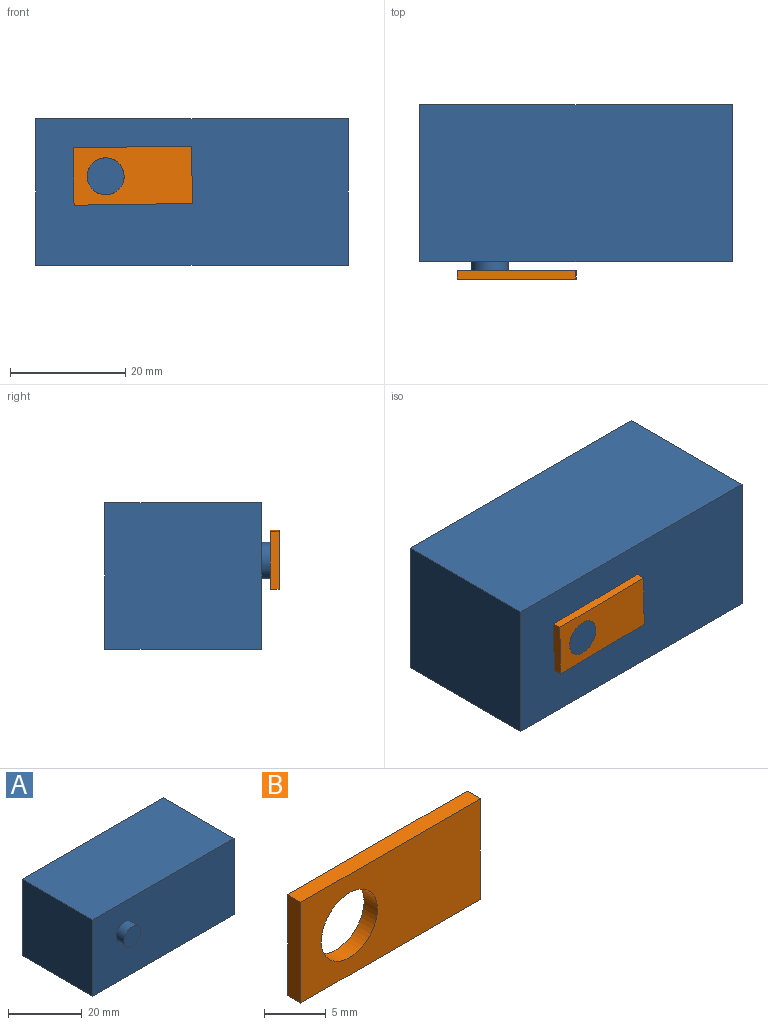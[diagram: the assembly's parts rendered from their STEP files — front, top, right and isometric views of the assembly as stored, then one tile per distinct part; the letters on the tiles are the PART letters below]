
ASSEMBLY  parts=2 mates=1
PART A: 8 faces, bbox 54.3x30.3x25.4 mm
  f0: plane 27.23x25.4mm, normal (-1,0,0), area 691.6mm2, adj f1,f3,f4,f5
  f1: plane 54.29x25.4mm, normal (0,-1,0), area 1346.6mm2, adj f0,f2,f4,f5,f6
  f2: plane 27.23x25.4mm, normal (1,0,0), area 691.6mm2, adj f1,f3,f4,f5
  f3: plane 54.29x25.4mm, normal (0,1,0), area 1379mm2, adj f0,f2,f4,f5
  f4: plane 54.29x27.23mm, normal (0,0,1), area 1478.3mm2, adj f0,f1,f2,f3
  f5: plane 54.29x27.23mm, normal (0,0,-1), area 1478.3mm2, adj f0,f1,f2,f3
  f6: cylinder r=3.21mm len=6.42mm, axis (0,1,0), area 61.5mm2, adj f1,f7
  f7: plane 6.42x6.42mm, normal (0,-1,0), area 32.4mm2, adj f6
PART B: 7 faces, bbox 20.6x1.5x10 mm
  f0: plane 20.55x1.52mm, normal (0,0,1), area 31.3mm2, adj f1,f4,f5,f6
  f1: plane 9.97x1.52mm, normal (-1,0,0), area 15.2mm2, adj f0,f2,f5,f6
  f2: plane 20.55x1.52mm, normal (0,0,-1), area 31.3mm2, adj f1,f4,f5,f6
  f3: cylinder r=3.21mm len=6.42mm, axis (0,1,0), area 30.7mm2, adj f5,f6
  f4: plane 9.97x1.52mm, normal (1,0,0), area 15.2mm2, adj f0,f2,f5,f6
  f5: plane 20.55x9.97mm, normal (0,-1,0), area 172.5mm2, adj f0,f1,f2,f3,f4
  f6: plane 20.55x9.97mm, normal (0,1,0), area 172.5mm2, adj f0,f1,f2,f3,f4
PLACE A t=(-9.38,24.05,-21.47)mm fixed
PLACE B rot(axis=(0,-1,0),0.8deg) t=(-9.16,24.31,-20.85)mm
MATE revolute B.f3 <-> A.f6  axis (0,-1,0) through (-51.53,-32.46,-6.05)mm
